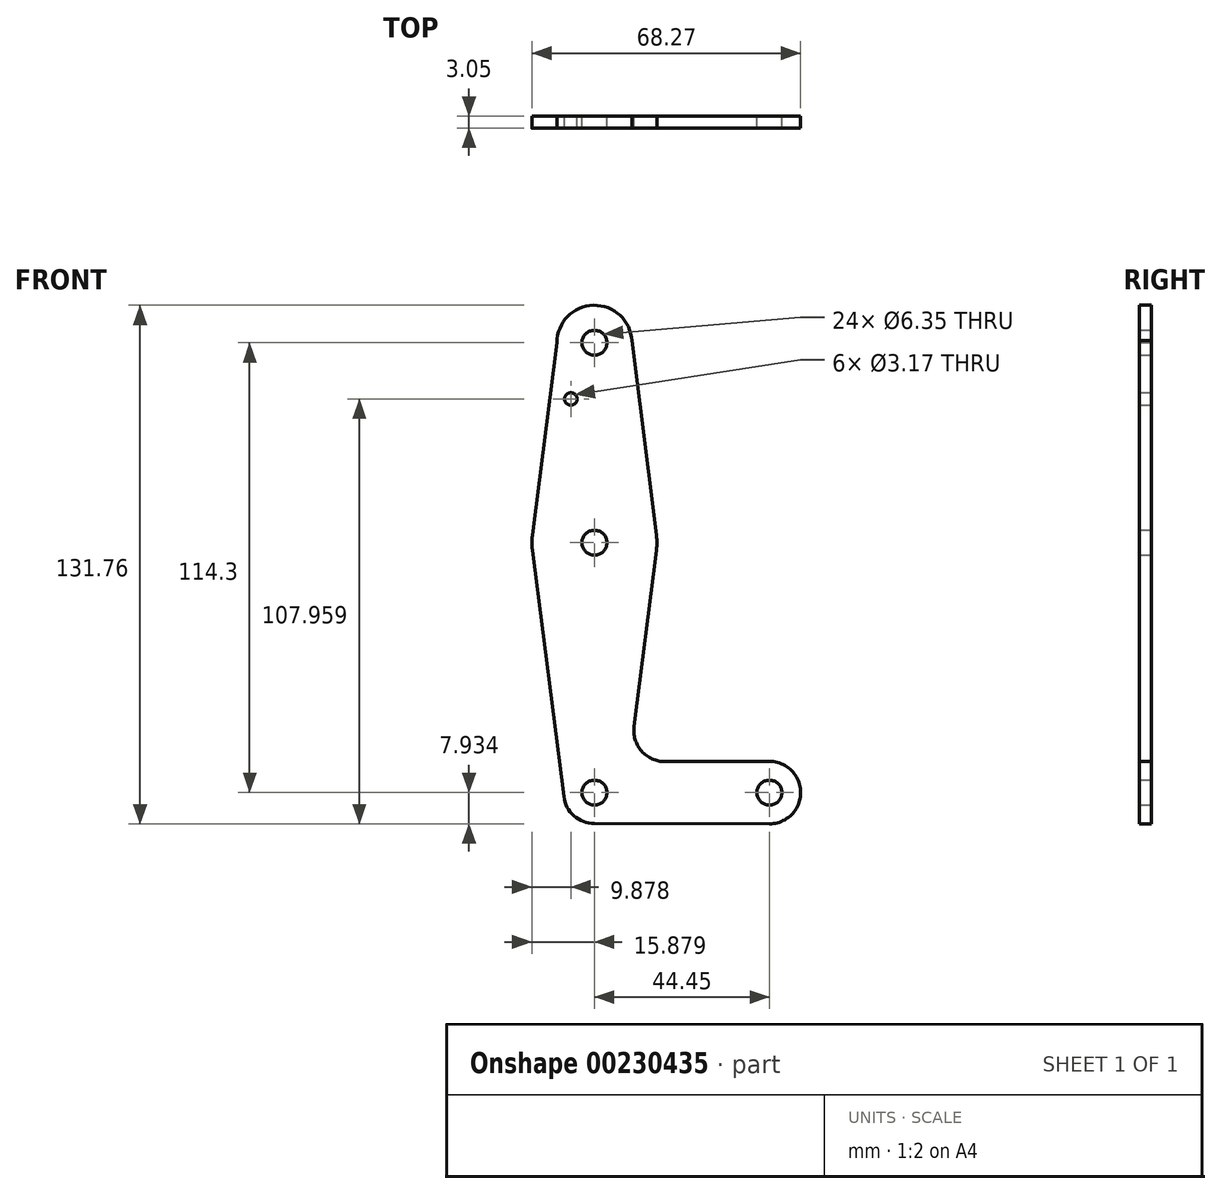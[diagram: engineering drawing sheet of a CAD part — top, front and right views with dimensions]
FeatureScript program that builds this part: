
annotation { "Feature Type Name" : "Feature", "Feature Type Description" : "" }
export const myFeature = defineFeature(function(context is Context, id is Id, definition is map)
    precondition{}
    {
        {
            var Q0;
            Q0=qCreatedBy(makeId("Front.planeOp"),FACE);
            var sketch = newSketch(context, id + "F0", { "sketchPlane" : qUnion([Q0])});
            skLineSegment(sketch, "E0", {"start": v(-39.03, 94.4) * mm, "end": v(-39.03, -19.9) * mm, "construction": true});
            skLineSegment(sketch, "E1", {"start": v(-39.03, -19.9) * mm, "end": v(5.42, -19.9) * mm, "construction": true});
            skCircle(sketch, "E2", {"center": v(-39.03, 94.4) * mm, "radius": 9.53 * mm});
            skCircle(sketch, "E3", {"center": v(-39.03, 43.6) * mm, "radius": 15.88 * mm});
            skCircle(sketch, "E4", {"center": v(-39.03, -19.9) * mm, "radius": 7.84 * mm});
            skCircle(sketch, "E5", {"center": v(5.42, -19.9) * mm, "radius": 7.94 * mm});
            skLineSegment(sketch, "E6", {"start": v(-39.03, -27.75) * mm, "end": v(5.4, -27.84) * mm});
            skLineSegment(sketch, "E7", {"start": v(-21.07, -12.02) * mm, "end": v(5.4, -11.97) * mm});
            skLineSegment(sketch, "E8", {"start": v(-29.52, 94.9) * mm, "end": v(-23.28, 45.59) * mm});
            skLineSegment(sketch, "E9", {"start": v(-23.28, 41.59) * mm, "end": v(-28.98, -3.07) * mm});
            skLineSegment(sketch, "E10", {"start": v(-48.56, 94.4) * mm, "end": v(-54.78, 45.6) * mm});
            skLineSegment(sketch, "E11", {"start": v(-54.78, 41.59) * mm, "end": v(-46.81, -20.9) * mm});
            skCircle(sketch, "E12", {"center": v(-39.03, 94.4) * mm, "radius": 3.18 * mm});
            skCircle(sketch, "E13", {"center": v(-39.03, 43.6) * mm, "radius": 3.18 * mm});
            skCircle(sketch, "E14", {"center": v(-39.03, -19.9) * mm, "radius": 3.18 * mm});
            skCircle(sketch, "E15", {"center": v(5.42, -19.9) * mm, "radius": 3.18 * mm});
            skCircle(sketch, "E16", {"center": v(-45.03, 80.12) * mm, "radius": 1.59 * mm});
            skPoint(sketch, "E17.newPointB", {"position": v(-39.03, -12.06) * mm});
            skArc(sketch, "E17.filletArc", {"start": v(-28.98, -3.07) * mm, "mid": v(-27.05, -9.33) * mm, "end": v(-21.07, -12.02) * mm});
            skSolve(sketch);
        }
        {
            var Q0;
            Q0 = qSketchRegion(id + "F0", true);
            extrude(context, id + "F1", {"entities" : qUnion([Q0]), "depth" : 3.05 * mm});
        }
    });
